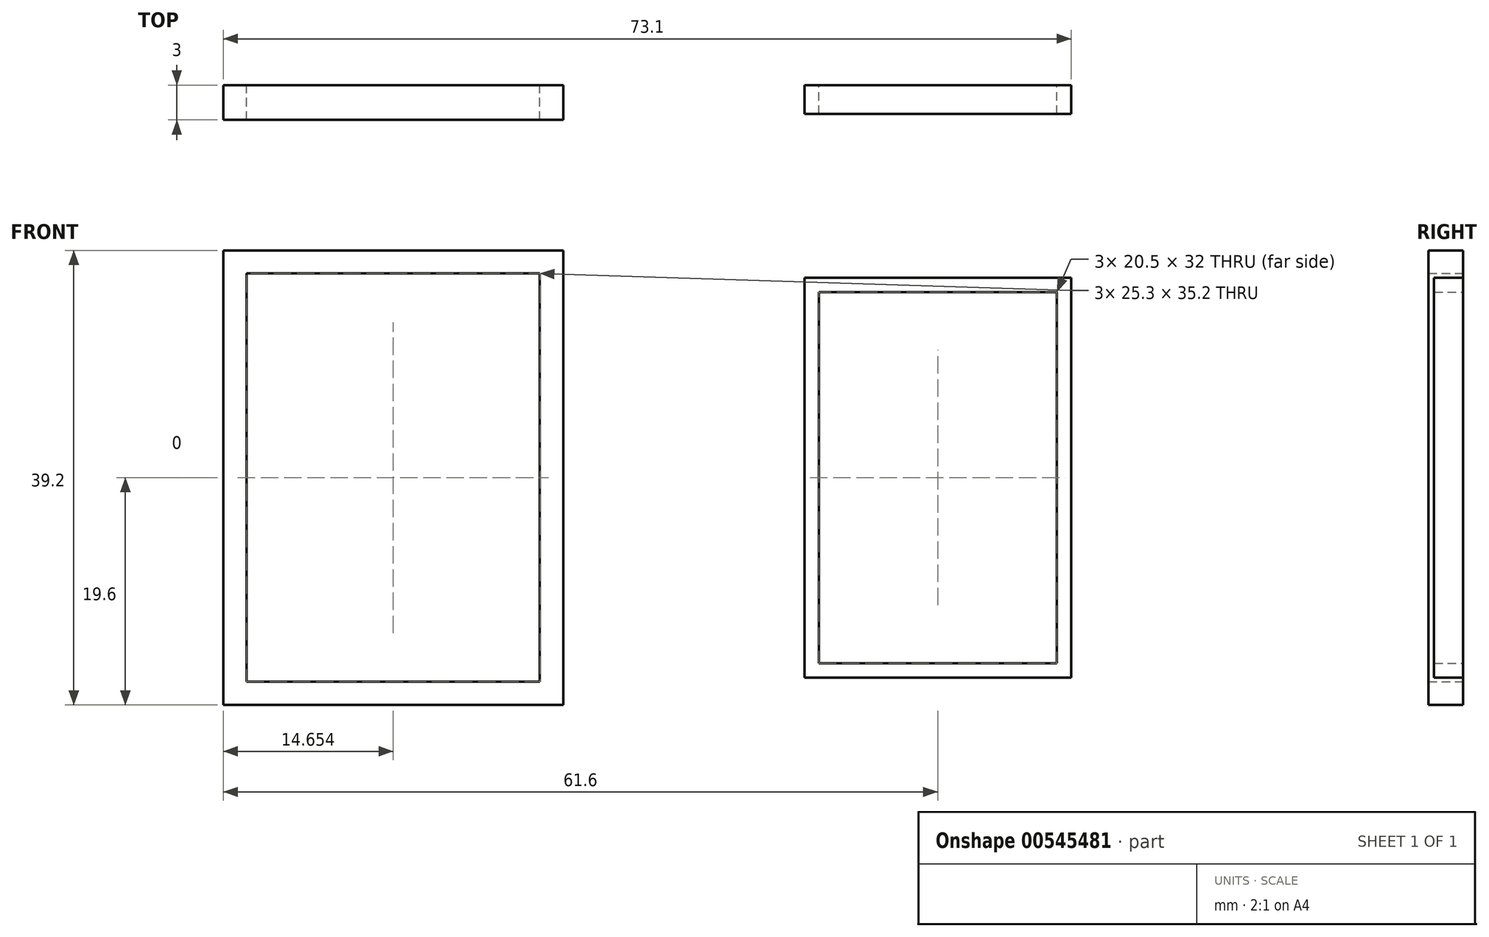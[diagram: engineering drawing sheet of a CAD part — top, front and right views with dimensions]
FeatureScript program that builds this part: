
annotation { "Feature Type Name" : "Feature", "Feature Type Description" : "" }
export const myFeature = defineFeature(function(context is Context, id is Id, definition is map)
    precondition{}
    {
        {
            var Q0;
            Q0=qCreatedBy(makeId("Front.planeOp"),FACE);
            var sketch = newSketch(context, id + "F0", { "sketchPlane" : qUnion([Q0])});
            skPoint(sketch, "E0.middle", {"position": v(0, 0) * mm});
            skLineSegment(sketch, "E1.bottom", {"start": v(11.5, -17.25) * mm, "end": v(-11.5, -17.25) * mm});
            skLineSegment(sketch, "E1.top", {"start": v(11.5, 17.25) * mm, "end": v(-11.5, 17.25) * mm});
            skLineSegment(sketch, "E1.left", {"start": v(11.5, -17.25) * mm, "end": v(11.5, 17.25) * mm});
            skLineSegment(sketch, "E1.right", {"start": v(-11.5, -17.25) * mm, "end": v(-11.5, 17.25) * mm});
            skLineSegment(sketch, "E2.bottom", {"start": v(10.25, -16) * mm, "end": v(-10.25, -16) * mm});
            skLineSegment(sketch, "E2.top", {"start": v(10.25, 16) * mm, "end": v(-10.25, 16) * mm});
            skLineSegment(sketch, "E2.left", {"start": v(10.25, -16) * mm, "end": v(10.25, 16) * mm});
            skLineSegment(sketch, "E2.right", {"start": v(-10.25, -16) * mm, "end": v(-10.25, 16) * mm});
            skSolve(sketch);
        }
        {
            var Q0;
            Q0=makeQuery(id+"F0.imprint","IMPRINT",FACE,{"disambiguationData":[TD([[makeQuery(id+"F0.imprint","IMPRINT",EDGE,{"derivedFrom":sQuery(id+"F0.wireOp",EDGE,"E1.bottom")}),-1.0]])]});
            extrude(context, id + "F1", {"entities" : qUnion([Q0]), "depth" : 2.5 * mm, "offsetDistance" : 25 * mm});
        }
        {
            var Q0;
            Q0=qCreatedBy(makeId("Front.planeOp"),FACE);
            var sketch = newSketch(context, id + "F2", { "sketchPlane" : qUnion([Q0])});
            skLineSegment(sketch, "E3.bottom", {"start": v(-32.3, -19.6) * mm, "end": v(-61.6, -19.6) * mm});
            skLineSegment(sketch, "E3.top", {"start": v(-32.3, 19.6) * mm, "end": v(-61.6, 19.6) * mm});
            skLineSegment(sketch, "E3.left", {"start": v(-32.3, -19.6) * mm, "end": v(-32.3, 19.6) * mm});
            skLineSegment(sketch, "E3.right", {"start": v(-61.6, -19.6) * mm, "end": v(-61.6, 19.6) * mm});
            skPoint(sketch, "E3.middle", {"position": v(-46.95, 0) * mm});
            skLineSegment(sketch, "E4.bottom", {"start": v(-59.6, -17.6) * mm, "end": v(-34.3, -17.6) * mm});
            skLineSegment(sketch, "E4.top", {"start": v(-59.6, 17.6) * mm, "end": v(-34.3, 17.6) * mm});
            skLineSegment(sketch, "E4.left", {"start": v(-59.6, -17.6) * mm, "end": v(-59.6, 17.6) * mm});
            skLineSegment(sketch, "E4.right", {"start": v(-34.3, -17.6) * mm, "end": v(-34.3, 17.6) * mm});
            skSolve(sketch);
        }
        {
            var Q0;
            Q0=makeQuery(id+"F2.imprint","IMPRINT",FACE,{"disambiguationData":[TD([[makeQuery(id+"F2.imprint","IMPRINT",EDGE,{"derivedFrom":sQuery(id+"F2.wireOp",EDGE,"E3.bottom")}),-1.0]])]});
            extrude(context, id + "F3", {"entities" : qUnion([Q0]), "depth" : 3 * mm, "offsetDistance" : 25 * mm});
        }
    });
